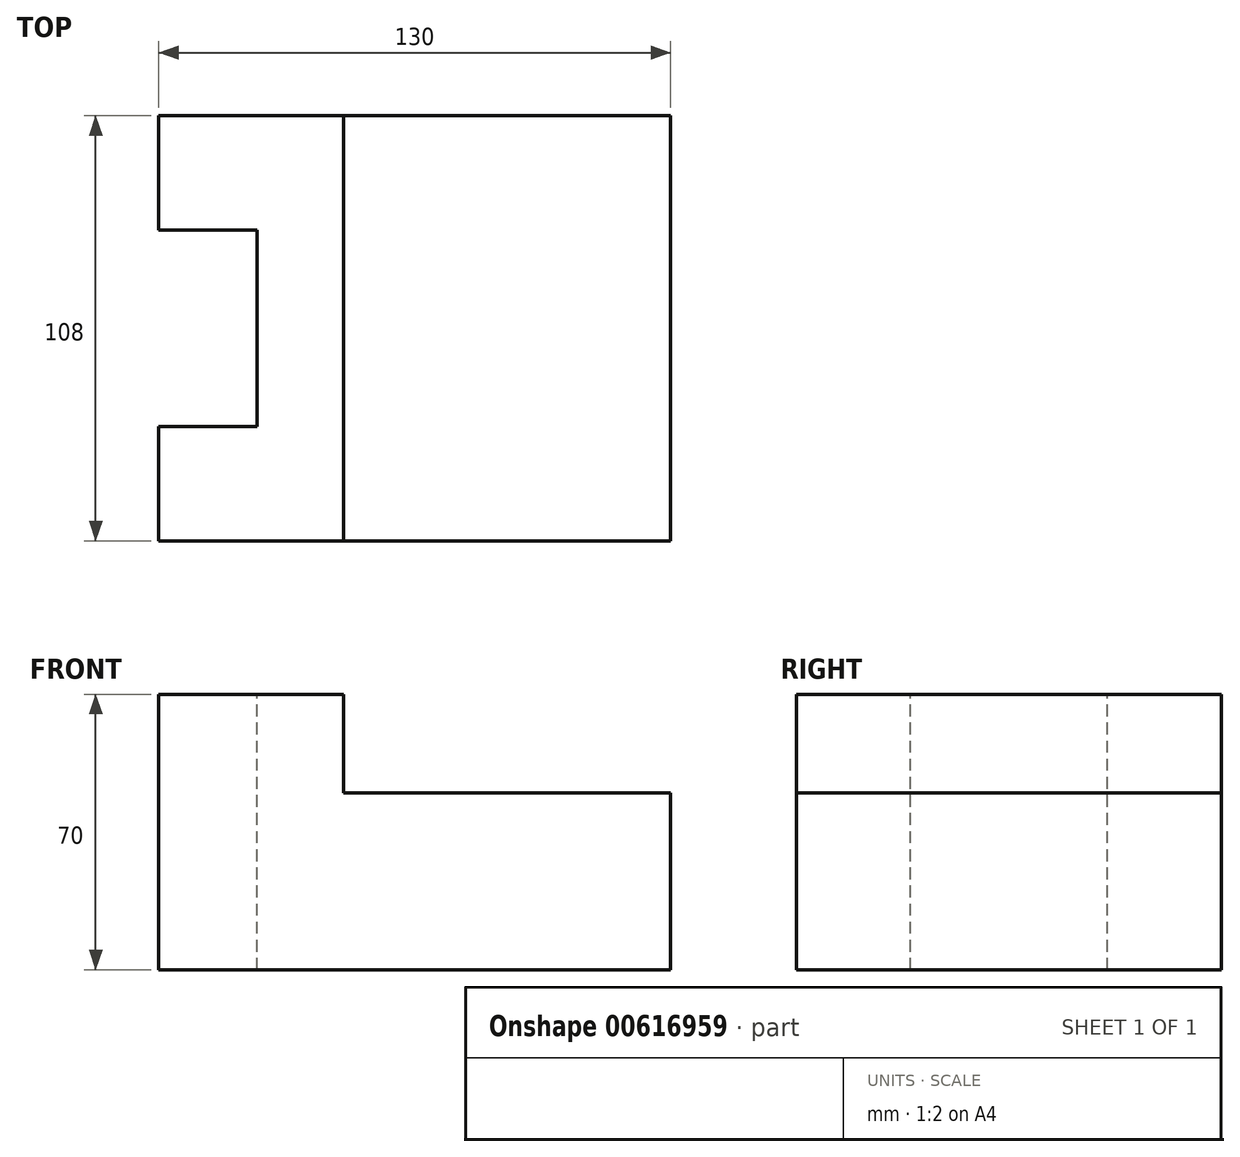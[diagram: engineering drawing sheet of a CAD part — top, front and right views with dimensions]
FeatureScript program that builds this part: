
annotation { "Feature Type Name" : "Feature", "Feature Type Description" : "" }
export const myFeature = defineFeature(function(context is Context, id is Id, definition is map)
    precondition{}
    {
        {
            var Q0;
            Q0=qCreatedBy(makeId("Top.planeOp"),FACE);
            var sketch = newSketch(context, id + "F0", { "sketchPlane" : qUnion([Q0])});
            skLineSegment(sketch, "E0.bottom", {"start": v(65, -54) * mm, "end": v(-65, -54) * mm});
            skLineSegment(sketch, "E0.top", {"start": v(65, 54) * mm, "end": v(-65, 54) * mm});
            skLineSegment(sketch, "E0.left", {"start": v(65, -54) * mm, "end": v(65, 54) * mm});
            skLineSegment(sketch, "E0.right", {"start": v(-65, -54) * mm, "end": v(-65, 54) * mm});
            skPoint(sketch, "E0.middle", {"position": v(0, 0) * mm});
            skSolve(sketch);
        }
        {
            var Q0;
            Q0=makeQuery(id+"F0.imprint","IMPRINT",FACE,{"disambiguationData":[TD([[makeQuery(id+"F0.imprint","IMPRINT",EDGE,{"derivedFrom":sQuery(id+"F0.wireOp",EDGE,"E0.bottom")}),-1.0]])]});
            extrude(context, id + "F1", {"entities" : qUnion([Q0]), "depth" : 45 * mm, "offsetDistance" : 25 * mm});
        }
        {
            var Q0;
            Q0=makeQuery(id+"F1.opExtrude","SWEPT_FACE",FACE,{"disambiguationData":[OSD([sQuery(id+"F0.wireOp",EDGE,"E0.right")])]});
            var sketch = newSketch(context, id + "F2", { "sketchPlane" : qUnion([Q0])});
            skLineSegment(sketch, "E1.bottom", {"start": v(-54, 45) * mm, "end": v(54, 45) * mm});
            skLineSegment(sketch, "E1.top", {"start": v(-54, 70) * mm, "end": v(54, 70) * mm});
            skLineSegment(sketch, "E1.left", {"start": v(-54, 45) * mm, "end": v(-54, 70) * mm});
            skLineSegment(sketch, "E1.right", {"start": v(54, 45) * mm, "end": v(54, 70) * mm});
            skSolve(sketch);
        }
        {
            var Q0;
            Q0 = qSketchRegion(id + "F2", true);
            extrude(context, id + "F3", {"entities" : qUnion([Q0]), "operationType" : NewBodyOperationType.ADD, "oppositeDirection" : true, "depth" : 47 * mm, "offsetDistance" : 25 * mm});
        }
        {
            var Q0;
            Q0=makeQuery(id+"F3.opExtrude","SWEPT_FACE",FACE,{"disambiguationData":[OSD([sQuery(id+"F2.wireOp",EDGE,"E1.top")])]});
            var sketch = newSketch(context, id + "F4", { "sketchPlane" : qUnion([Q0])});
            skLineSegment(sketch, "E2.bottom", {"start": v(-65, 25) * mm, "end": v(-40, 25) * mm});
            skLineSegment(sketch, "E2.top", {"start": v(-65, -25) * mm, "end": v(-40, -25) * mm});
            skLineSegment(sketch, "E2.left", {"start": v(-65, 25) * mm, "end": v(-65, -25) * mm});
            skLineSegment(sketch, "E2.right", {"start": v(-40, 25) * mm, "end": v(-40, -25) * mm});
            skSolve(sketch);
        }
        {
            var Q0;
            Q0 = qSketchRegion(id + "F4", true);
            extrude(context, id + "F5", {"entities" : qUnion([Q0]), "operationType" : NewBodyOperationType.REMOVE, "endBound" : BoundingType.THROUGH_ALL, "oppositeDirection" : true, "depth" : 25 * mm, "offsetDistance" : 25 * mm});
        }
    });
